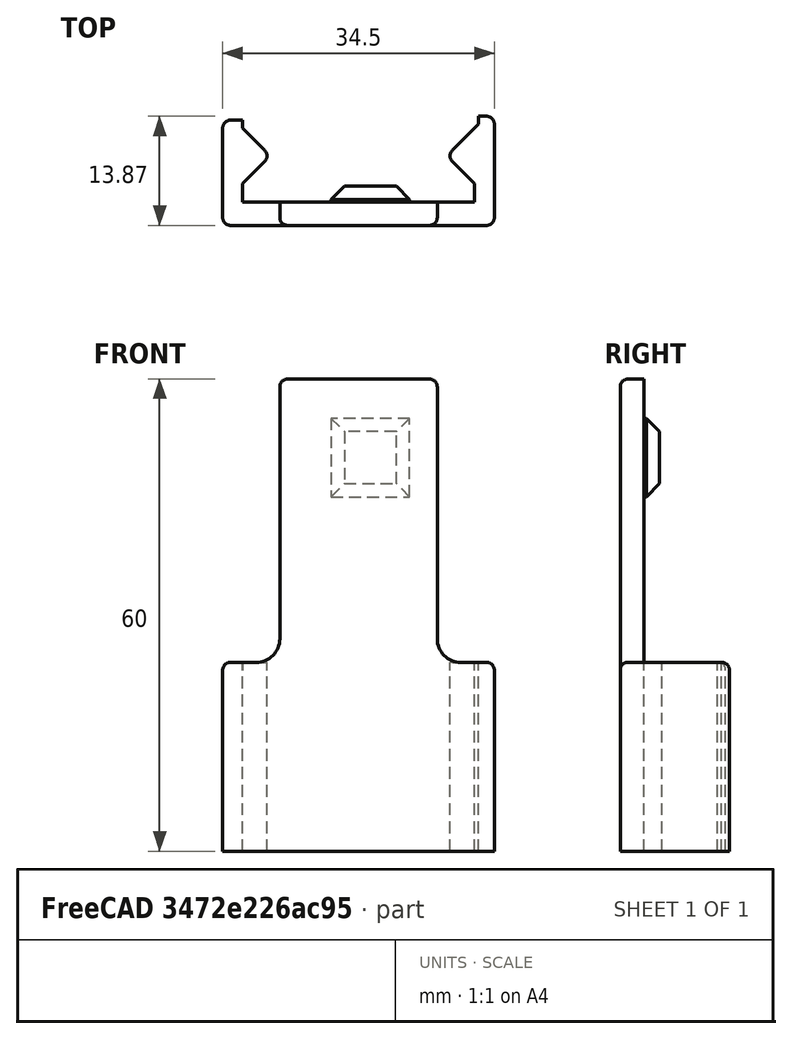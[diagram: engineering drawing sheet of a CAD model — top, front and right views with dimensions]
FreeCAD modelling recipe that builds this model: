
FCSTD DOCUMENT  (FreeCAD 0.19R)
Label: Latch
License: All rights reserved
LicenseURL: http://en.wikipedia.org/wiki/All_rights_reserved
objects: PartDesign::Fillet×7, Sketcher::SketchObject×3, PartDesign::Pad×2, PartDesign::Chamfer×2, PartDesign::Pocket×1, PartDesign::Body×1, Mesh::Feature×1
note: 28 computed .brp shape members not serialized (recipe doc carries the construction recipe); baked Part::Feature solids carry a one-line shape summary decoded from their .brp

FEATURE [Sketcher::SketchObject] Sketch
  FullyConstrained = true
  MapMode = 5
  Support = -> [XY_Plane]
  sketch-geometry (14):
    g0: LineSegment StartX=-17.25 StartY=0 StartZ=0 EndX=17.25 EndY=0 EndZ=0
    g1: LineSegment StartX=17.25 StartY=0 StartZ=0 EndX=17.25 EndY=14.0711 EndZ=0
    g2: LineSegment StartX=14.75 StartY=3 StartZ=0 EndX=-14.75 EndY=3 EndZ=0
    g3: LineSegment StartX=-17.25 StartY=13.5711 StartZ=0 EndX=-17.25 EndY=0 EndZ=0
    g4: LineSegment StartX=14.75 StartY=3 StartZ=0 EndX=14.75 EndY=5.5 EndZ=0
    g5: LineSegment StartX=14.75 StartY=5.5 StartZ=0 EndX=11.2145 EndY=9.03553 EndZ=0
    g6: LineSegment StartX=11.2145 StartY=9.03553 StartZ=0 EndX=15.25 EndY=13.0711 EndZ=0
    g7: LineSegment StartX=15.25 StartY=13.0711 StartZ=0 EndX=15.25 EndY=14.0711 EndZ=0
    g8: LineSegment StartX=-14.75 StartY=3 StartZ=0 EndX=-14.75 EndY=5.5 EndZ=0
    g9: LineSegment StartX=-14.75 StartY=5.5 StartZ=0 EndX=-11.2145 EndY=9.03553 EndZ=0
    g10: LineSegment StartX=-11.2145 StartY=9.03553 StartZ=0 EndX=-14.75 EndY=12.5711 EndZ=0
    g11: LineSegment StartX=-14.75 StartY=12.5711 StartZ=0 EndX=-14.75 EndY=13.5711 EndZ=0
    g12: LineSegment StartX=-17.25 StartY=13.5711 StartZ=0 EndX=-14.75 EndY=13.5711 EndZ=0
    g13: LineSegment StartX=15.25 StartY=14.0711 StartZ=0 EndX=17.25 EndY=14.0711 EndZ=0
  constraints (40):
    c: PointOnObject(g0,g-1)
    c: Coincident(g0,g1)
    c: Vertical(g1)
    c: Coincident(g3,g0)
    c: Vertical(g3)
    c: Symmetric(g2,g2,g-2)
    c: Symmetric(g0,g0,g-2)
    c: Coincident(g2,g4)
    c: Coincident(g4,g5)
    c: Coincident(g5,g6)
    c: Coincident(g6,g7)
    c: Coincident(g2,g8)
    c: Coincident(g8,g9)
    c: Coincident(g9,g10)
    c: Coincident(g10,g11)
    c: Vertical(g7)
    c: Vertical(g11)
    c: Vertical(g8)
    c: Vertical(g4)
    c: Angle(g9) = 0.785398
    c: Angle(g6) = 0.785398
    c: Perpendicular(g9,g10)
    c: Perpendicular(g6,g5)
    c: Equal(g4,g8)
    c: Equal(g11,g7)
    c: Equal(g9,g10)
    c: Distance(g2) = 29.5
    c: Distance(g2,g1) = 2.5
    c: DistanceY(g2) = 3
    c: Distance(g4) = 2.5
    c: Coincident(g12,g3)
    c: Coincident(g12,g11)
    c: Coincident(g13,g7)
    c: Coincident(g13,g1)
    c: Horizontal(g13)
    c: Horizontal(g12)
    c: Distance(g13) = 2
    c: Distance(g7) = 1
    c: Distance(g5) = 5
    c: Distance(g9) = 5
FEATURE [PartDesign::Pad] Pad
  Direction = (1,1,1)
  Length = 60
  Length2 = 100
  Profile = -> Sketch
  Type = 0
FEATURE [Sketcher::SketchObject] Sketch001
  FullyConstrained = true
  MapMode = 5
  Placement = pos=(0,0,0) rot=(1,0,0;1.5708rad)
  Support = -> [Pad]
  sketch-geometry (12):
    g0: LineSegment StartX=10 StartY=65 StartZ=0 EndX=10 EndY=24 EndZ=0
    g1: LineSegment StartX=10 StartY=24 StartZ=0 EndX=17.55 EndY=24 EndZ=0
    g2: LineSegment StartX=17.55 StartY=24 StartZ=0 EndX=17.55 EndY=0 EndZ=0
    g3: LineSegment StartX=-17.55 StartY=0 StartZ=0 EndX=-17.55 EndY=24 EndZ=0
    g4: LineSegment StartX=-17.55 StartY=24 StartZ=0 EndX=-10 EndY=24 EndZ=0
    g5: LineSegment StartX=-10 StartY=24 StartZ=0 EndX=-10 EndY=65 EndZ=0
    g6: LineSegment StartX=-10 StartY=65 StartZ=0 EndX=10 EndY=65 EndZ=0
    g7: LineSegment StartX=17.55 StartY=0 StartZ=0 EndX=44.27 EndY=0 EndZ=0
    g8: LineSegment StartX=44.27 StartY=0 StartZ=0 EndX=44.27 EndY=69.33 EndZ=0
    g9: LineSegment StartX=44.27 StartY=69.33 StartZ=0 EndX=-44.27 EndY=69.33 EndZ=0
    g10: LineSegment StartX=-44.27 StartY=69.33 StartZ=0 EndX=-44.27 EndY=0 EndZ=0
    g11: LineSegment StartX=-44.27 StartY=0 StartZ=0 EndX=-17.55 EndY=0 EndZ=0
  constraints (34):
    c: Vertical(g0)
    c: Coincident(g0,g1)
    c: Coincident(g1,g2)
    c: Coincident(g3,g4)
    c: Coincident(g4,g5)
    c: Coincident(g5,g6)
    c: Coincident(g6,g0)
    c: Horizontal(g6)
    c: Symmetric(g0,g4,g-2)
    c: Vertical(g5)
    c: Angle(g1) = 0
    c: Vertical(g2)
    c: Vertical(g3)
    c: Symmetric(g1,g3,g-2)
    c: PointOnObject(g2,g-1)
    c: Distance(g2) = 24
    c: Distance(g0,g4) = 20
    c: Distance(g0) = 41
    c: Coincident(g2,g7)
    c: Horizontal(g7)
    c: Coincident(g7,g8)
    c: Vertical(g8)
    c: Coincident(g8,g9)
    c: Horizontal(g9)
    c: Coincident(g9,g10)
    c: Vertical(g10)
    c: Coincident(g10,g11)
    c: Coincident(g11,g3)
    c: Horizontal(g11)
    c: PointOnObject(g3,g-1)
    c: Distance(g11) = 26.72
    c: Equal(g7,g11)
    c: Distance(g2,g3) = 35.1
    c: Distance(g8) = 69.33
FEATURE [PartDesign::Pocket] Pocket
  BaseFeature = -> Pad
  Length = 5
  Length2 = 100
  Profile = -> Sketch001
  Type = 1
FEATURE [Sketcher::SketchObject] Sketch002
  FullyConstrained = false
  MapMode = 5
  Placement = pos=(0,3,0) rot=(0,0.707107,0.707107;3.14159rad)
  Support = -> [Pocket]
  sketch-geometry (4):
    g0: LineSegment StartX=-6.5 StartY=55 StartZ=0 EndX=3.5 EndY=55 EndZ=0
    g1: LineSegment StartX=3.5 StartY=55 StartZ=0 EndX=3.5 EndY=45 EndZ=0
    g2: LineSegment StartX=3.5 StartY=45 StartZ=0 EndX=-6.5 EndY=44.9987 EndZ=0
    g3: LineSegment StartX=-6.5 StartY=44.9987 StartZ=0 EndX=-6.5 EndY=55 EndZ=0
  constraints (11):
    c: Coincident(g0,g1)
    c: Coincident(g1,g2)
    c: Coincident(g2,g3)
    c: Coincident(g3,g0)
    c: Horizontal(g0)
    c: Vertical(g1)
    c: Vertical(g3)
    c: Equal(g2,g1)
    c: Distance(g2) = 10
    c: DistanceY(g1) = 45
    c: DistanceX(g1) = 3.5
FEATURE [PartDesign::Pad] Pad001
  BaseFeature = -> Pocket
  Direction = (1,1,1)
  Length = 2
  Length2 = 100
  Profile = -> Sketch002
  Type = 0
FEATURE [PartDesign::Chamfer] Chamfer
  Angle = 45
  Base = -> Pad001 [Face25]
  BaseFeature = -> Pad001
  ChamferType = 0
  FlipDirection = false
  Size = 1.7
  Size2 = 1
  SupportTransform = false
FEATURE [PartDesign::Fillet] Fillet
  Base = -> Chamfer [Edge54,Edge52]
  BaseFeature = -> Chamfer
  Radius = 3
  SupportTransform = false
FEATURE [PartDesign::Chamfer] Chamfer001
  Angle = 45
  Base = -> Fillet [Edge6]
  BaseFeature = -> Fillet
  ChamferType = 0
  FlipDirection = false
  Size = 2
  Size2 = 1
  SupportTransform = false
FEATURE [PartDesign::Fillet] Fillet001
  Base = -> Fillet [Edge70,Edge68]
  BaseFeature = -> Fillet
  Radius = 1
  SupportTransform = false
FEATURE [PartDesign::Fillet] Fillet002
  Base = -> Fillet001 [Edge43,Edge39]
  BaseFeature = -> Fillet001
  Radius = 1
  SupportTransform = false
FEATURE [PartDesign::Fillet] Fillet003
  Base = -> Fillet002 [Edge48,Edge30]
  BaseFeature = -> Fillet002
  Radius = 1
  SupportTransform = false
FEATURE [PartDesign::Fillet] Fillet004
  Base = -> Fillet003 [Edge20]
  BaseFeature = -> Fillet003
  Radius = 1
  SupportTransform = false
FEATURE [PartDesign::Fillet] Fillet005
  Base = -> Fillet004 [Edge104]
  BaseFeature = -> Fillet004
  Radius = 1
  SupportTransform = false
FEATURE [PartDesign::Fillet] Fillet006
  Base = -> Fillet005 [Edge34]
  BaseFeature = -> Fillet005
  Radius = 1
  SupportTransform = false
FEATURE [PartDesign::Body] Body
  Group = -> [Sketch,Pad,Sketch001,Pocket,Sketch002,Pad001,Chamfer,Fillet,Chamfer001,Fillet001,Fillet002,Fillet003,Fillet004,Fillet005,Fillet006]
  Origin = -> Origin
  Tip = -> Fillet006
FEATURE [Mesh::Feature] Mesh  label="Fillet006 (Meshed)"
